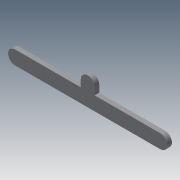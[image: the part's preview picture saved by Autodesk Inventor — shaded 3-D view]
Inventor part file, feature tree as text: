
AUTODESK INVENTOR PART (.ipt)
format: ipt  version: 2013 (Build 170138000, 138)  size: 154,624 bytes
history: native  units: mm
features: extrude x4, sketch x4
ambient origin geometry x8: Origin, YZ Plane, XZ Plane, XY Plane, X Axis, Y Axis, Z Axis, Center Point
bodies: Solid1 (feature_tree)
feature tree (8):
  extrude  "Extrusion1"  Depth=6.0mm
  extrude  "Extrusion2"  Depth=10.0mm
  extrude  "Extrusion3"  Depth=12.5mm
  extrude  "Extrusion4"  Depth=6.0mm
  sketch  "Sketch1"  dims[d0=18.0mm d1=6.0mm]
  sketch  "Sketch2"  dims[d2=10.0mm d3=10.0mm]
  sketch  "Sketch3"  dims[d4=12.5mm d5=12.5mm]
  sketch  "Sketch4"  dims[d6=6.0mm d7=6.0mm d8=0.01mm d9=6.0mm d10=0.01mm d11=6.0mm d12=0.01mm d13=6.0mm d14=0.01mm d15=6.0mm d16=0.01mm d17=0.01mm d18=2.0mm d19=0.0mm d20=3.0mm d21=3.0mm d22=3.0mm d23=1.5mm d24=3.0mm d25=3.0mm d26=2.0mm d27=0.0mm d28=0.01mm d29=0.01mm d30=2.0mm d31=0.0mm d32=0.01mm d33=2.0mm d34=0.0mm]
